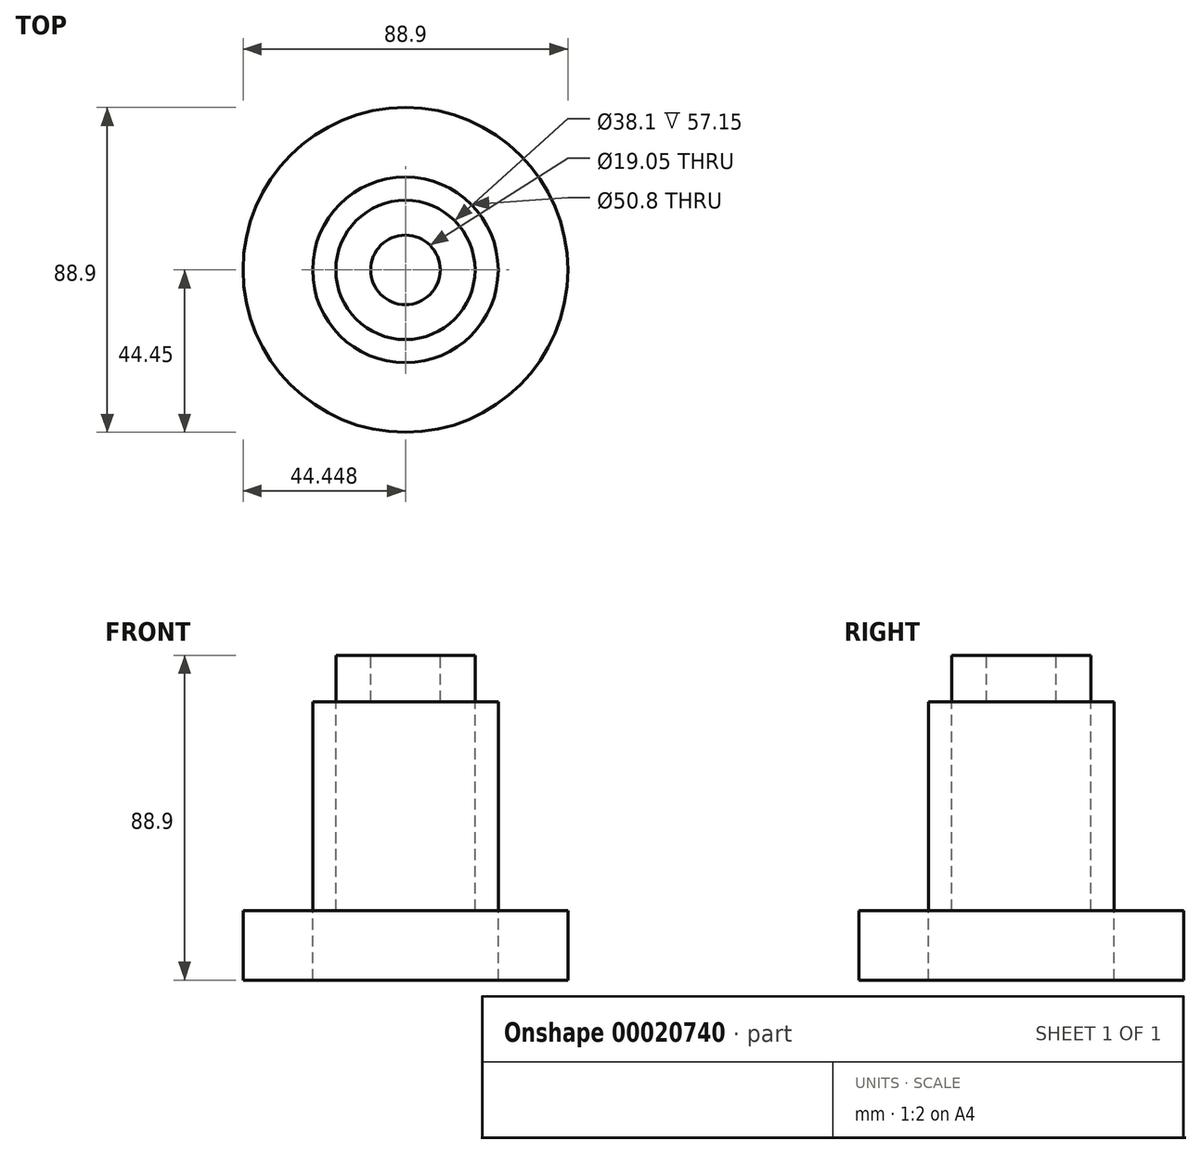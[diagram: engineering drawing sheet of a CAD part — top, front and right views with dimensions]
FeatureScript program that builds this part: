
annotation { "Feature Type Name" : "Feature", "Feature Type Description" : "" }
export const myFeature = defineFeature(function(context is Context, id is Id, definition is map)
    precondition{}
    {
        {
            var Q0;
            Q0=qCreatedBy(makeId("Front.planeOp"),FACE);
            var sketch = newSketch(context, id + "F0", { "sketchPlane" : qUnion([Q0])});
            skLineSegment(sketch, "E0", {"start": v(-11.71, -76.2) * mm, "end": v(7.34, -76.2) * mm});
            skLineSegment(sketch, "E1", {"start": v(7.34, -76.2) * mm, "end": v(7.34, -57.15) * mm});
            skLineSegment(sketch, "E2", {"start": v(-11.71, -76.2) * mm, "end": v(-11.71, -57.15) * mm});
            skLineSegment(sketch, "E3", {"start": v(-11.71, -57.15) * mm, "end": v(-11.71, 0) * mm});
            skLineSegment(sketch, "E4", {"start": v(-18.06, 0) * mm, "end": v(-18.06, 12.7) * mm});
            skLineSegment(sketch, "E5", {"start": v(-18.06, -57.15) * mm, "end": v(-18.06, 0) * mm});
            skLineSegment(sketch, "E6", {"start": v(-27.59, 0) * mm, "end": v(-27.59, 12.7) * mm});
            skLineSegment(sketch, "E7", {"start": v(-37.11, -57.15) * mm, "end": v(-37.11, -78.52) * mm});
            skLineSegment(sketch, "E8", {"start": v(-37.11, 0) * mm, "end": v(-37.11, -24.07) * mm});
            skLineSegment(sketch, "E9", {"start": v(-37.11, 12.7) * mm, "end": v(-37.11, 7.34) * mm});
            skLineSegment(sketch, "E10", {"start": v(-37.11, -57.15) * mm, "end": v(7.34, -57.15) * mm});
            skLineSegment(sketch, "E11", {"start": v(-37.11, 0) * mm, "end": v(-11.71, 0) * mm});
            skLineSegment(sketch, "E12", {"start": v(-37.11, 12.7) * mm, "end": v(-18.06, 12.7) * mm});
            skLineSegment(sketch, "E13", {"start": v(-37.11, 12.7) * mm, "end": v(-27.59, 12.7) * mm});
            skLineSegment(sketch, "E14", {"start": v(-11.71, 0) * mm, "end": v(-18.06, 0) * mm});
            skLineSegment(sketch, "E15", {"start": v(-18.06, 0) * mm, "end": v(-37.11, 0) * mm});
            skLineSegment(sketch, "E16", {"start": v(-37.11, -57.15) * mm, "end": v(-11.71, -57.15) * mm});
            skSolve(sketch);
        }
        {
            var Q0;
            Q0=makeQuery(id+"F0.imprint","IMPRINT",FACE,{"disambiguationData":[TD([[makeQuery(id+"F0.imprint","IMPRINT",EDGE,{"derivedFrom":sQuery(id+"F0.wireOp",EDGE,"E0")}),1.0]])]});
            var Q1;
            Q1=sQuery(id+"F0.wireOp",EDGE,"E7");
            revolve(context, id + "F1", {"entities" : qUnion([Q0]), "axis" : qUnion([Q1]), "revolveType" : RevolveType.FULL});
        }
        {
            var Q0;
            Q0=makeQuery(id+"F0.imprint","IMPRINT",FACE,{"disambiguationData":[TD([[makeQuery(id+"F0.imprint","IMPRINT",EDGE,{"derivedFrom":sQuery(id+"F0.wireOp",EDGE,"E3")}),1.0]])]});
            var Q1;
            Q1=sQuery(id+"F0.wireOp",EDGE,"E8");
            revolve(context, id + "F2", {"entities" : qUnion([Q0]), "axis" : qUnion([Q1]), "revolveType" : RevolveType.FULL});
        }
        {
            var Q0;
            Q0=makeQuery(id+"F0.imprint","IMPRINT",FACE,{"disambiguationData":[TD([[makeQuery(id+"F0.imprint","IMPRINT",EDGE,{"derivedFrom":sQuery(id+"F0.wireOp",EDGE,"E4")}),1.0]])]});
            var Q1;
            Q1=sQuery(id+"F0.wireOp",EDGE,"E9");
            revolve(context, id + "F3", {"entities" : qUnion([Q0]), "axis" : qUnion([Q1]), "revolveType" : RevolveType.FULL});
        }
    });
